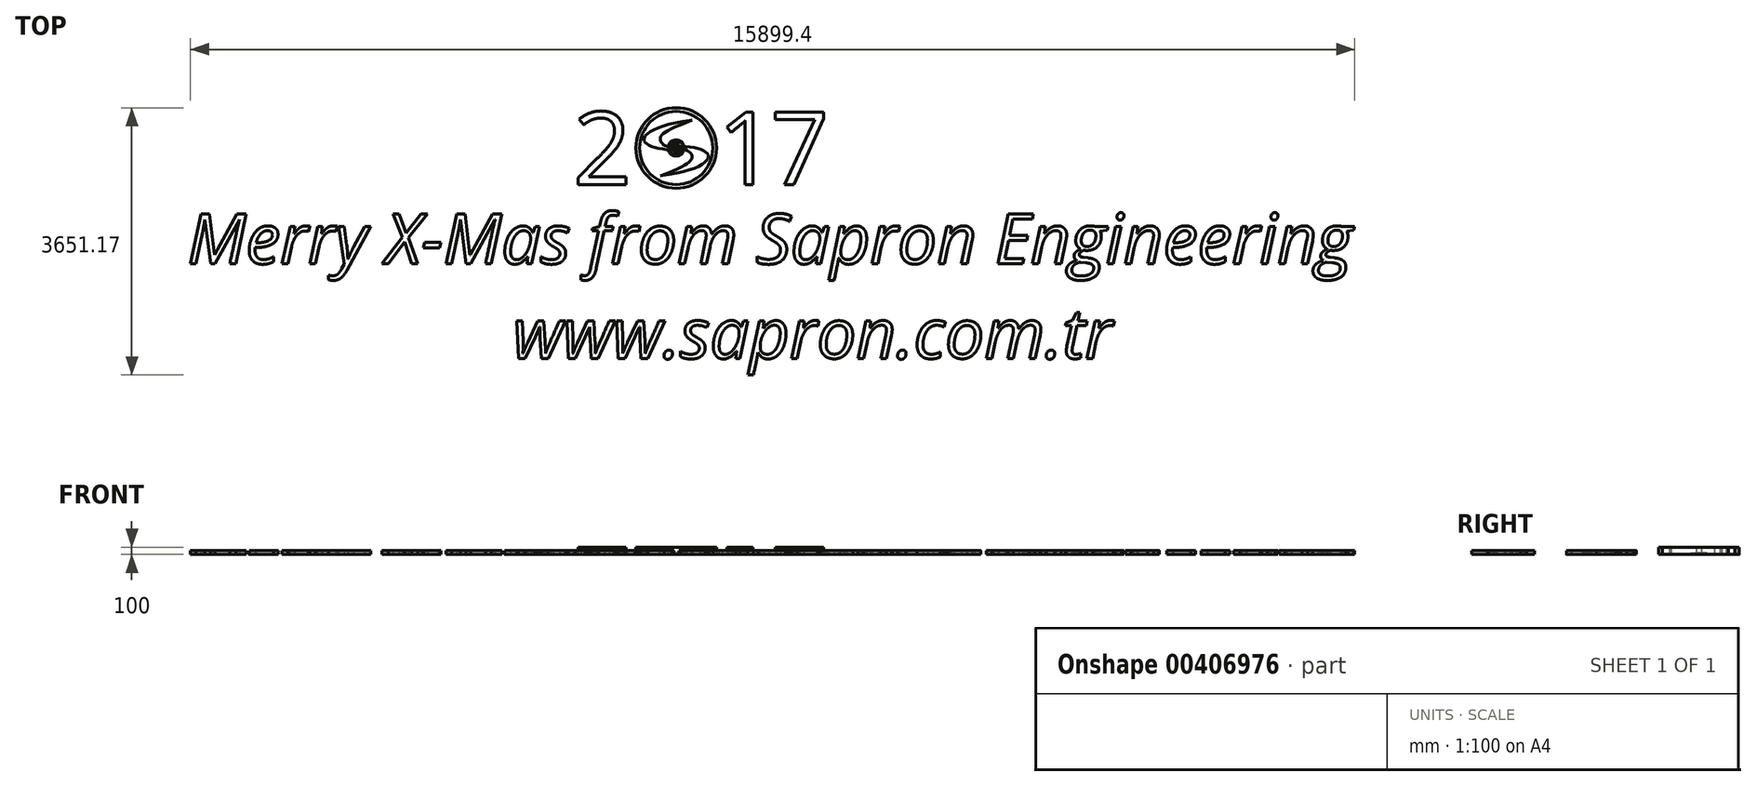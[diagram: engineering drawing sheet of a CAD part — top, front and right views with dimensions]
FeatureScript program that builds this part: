
annotation { "Feature Type Name" : "Feature", "Feature Type Description" : "" }
export const myFeature = defineFeature(function(context is Context, id is Id, definition is map)
    precondition{}
    {
        {
            var Q0;
            Q0=qCreatedBy(makeId("Top.planeOp"),FACE);
            var sketch = newSketch(context, id + "F0", { "sketchPlane" : qUnion([Q0])});
            skCircle(sketch, "E0", {"center": v(0, 0) * mm, "radius": 550 * mm});
            skCircle(sketch, "E1", {"center": v(0, 0) * mm, "radius": 500 * mm});
            skSolve(sketch);
        }
        {
            var Q0;
            Q0=qCreatedBy(makeId("Top.planeOp"),FACE);
            var sketch = newSketch(context, id + "F1", { "sketchPlane" : qUnion([Q0])});
            skText(sketch, "E2", { "text": "2", "fontName": "OpenSans-Regular.ttf"});
            skPoint(sketch, "E3", {"position": v(-1000, 0) * mm});
            const initialGuessF1  = {"E2": [-1.40484, -0.5, 1, 0, 1]};
            skSetInitialGuess(sketch, initialGuessF1);
            skSolve(sketch);
        }
        {
            var Q0;
            Q0=qCreatedBy(makeId("Top.planeOp"),FACE);
            var sketch = newSketch(context, id + "F2", { "sketchPlane" : qUnion([Q0])});
            skText(sketch, "E4", { "text": "1", "fontName": "OpenSans-Regular.ttf"});
            skPoint(sketch, "E5", {"position": v(850, 0) * mm});
            const initialGuessF2  = {"E4": [0.56257, -0.5, 1, 0, 1]};
            skSetInitialGuess(sketch, initialGuessF2);
            skSolve(sketch);
        }
        {
            var Q0;
            Q0=qCreatedBy(makeId("Top.planeOp"),FACE);
            var sketch = newSketch(context, id + "F3", { "sketchPlane" : qUnion([Q0])});
            skText(sketch, "E6", { "text": "7", "fontName": "OpenSans-Regular.ttf"});
            skPoint(sketch, "E7", {"position": v(1644.23, 0) * mm});
            skPoint(sketch, "E8", {"position": v(547.2, 0) * mm});
            skPoint(sketch, "E9", {"position": v(-547.73, 0) * mm});
            const initialGuessF3  = {"E6": [1.28743, -0.5, 1, 0, 1]};
            skSetInitialGuess(sketch, initialGuessF3);
            skSolve(sketch);
        }
        {
            var Q0;
            Q0=makeQuery(id+"F0.imprint","IMPRINT",FACE,{"disambiguationData":[TD([[makeQuery(id+"F0.imprint","IMPRINT",EDGE,{"derivedFrom":sQuery(id+"F0.wireOp",EDGE,"E0")}),1.0]])]});
            var Q1;
            Q1=makeQuery(id+"F1.imprint","IMPRINT",FACE,{"disambiguationData":[TD([[makeQuery(id+"F1.imprint","IMPRINT",EDGE,{"derivedFrom":sQuery(id+"F1.wireOp",EDGE,"E2.sketch_text.stroke-0")}),-1.0]])]});
            var Q2;
            Q2=makeQuery(id+"F2.imprint","IMPRINT",FACE,{"disambiguationData":[TD([[makeQuery(id+"F2.imprint","IMPRINT",EDGE,{"derivedFrom":sQuery(id+"F2.wireOp",EDGE,"E4.sketch_text.stroke-0")}),-1.0]])]});
            var Q3;
            Q3=makeQuery(id+"F3.imprint","IMPRINT",FACE,{"disambiguationData":[TD([[makeQuery(id+"F3.imprint","IMPRINT",EDGE,{"derivedFrom":sQuery(id+"F3.wireOp",EDGE,"E6.sketch_text.stroke-0")}),-1.0]])]});
            extrude(context, id + "F4", {"entities" : qUnion([Q0, Q1, Q2, Q3]), "depth" : 100 * mm});
        }
        {
            var Q0;
            Q0=qCreatedBy(makeId("Top.planeOp"),FACE);
            var sketch = newSketch(context, id + "F5", { "sketchPlane" : qUnion([Q0])});
            skPoint(sketch, "E10", {"position": v(235.96, 379.51) * mm});
            skPoint(sketch, "E11", {"position": v(-412.73, 89.64) * mm});
            skPoint(sketch, "E12", {"position": v(110.77, -36.28) * mm});
            skFitSpline(sketch, "E13", {"points": [v(235.96, 379.51) * mm, v(-412.73, 89.64) * mm, v(110.77, -36.28) * mm], "startDerivative": vector(-2842.12, -332.1) * mm, "endDerivative": vector(1785.84, -40.7) * mm});
            skPoint(sketch, "E14", {"position": v(-195.48, 106.23) * mm});
            skFitSpline(sketch, "E15", {"points": [v(235.96, 379.51) * mm, v(-195.48, 106.23) * mm, v(110.77, -36.28) * mm], "startDerivative": vector(-2236.59, -817.49) * mm, "endDerivative": vector(1737.9, -347.34) * mm});
            skSolve(sketch);
        }
        {
            var Q0;
            Q0=makeQuery(id+"F5.imprint","IMPRINT",FACE,{"disambiguationData":[TD([[makeQuery(id+"F5.imprint","IMPRINT",EDGE,{"derivedFrom":sQuery(id+"F5.wireOp",EDGE,"E13")}),1.0]])]});
            extrude(context, id + "F6", {"entities" : qUnion([Q0]), "depth" : 100 * mm});
        }
        {
            var Q0;
            Q0=qCreatedBy(makeId("Right.planeOp"),FACE);
            var sketch = newSketch(context, id + "F7", { "sketchPlane" : qUnion([Q0])});
            skLineSegment(sketch, "E16", {"start": v(0, 0) * mm, "end": v(0, -184.27) * mm});
            skSolve(sketch);
        }
        {
            var Q0;
            Q0=makeQuery(id+"F6.opExtrude","SWEPT_BODY",BODY,{"disambiguationData":[OSD([sQuery(id+"F5.wireOp",EDGE,"E13"),sQuery(id+"F5.wireOp",EDGE,"E15")])]});
            var Q1;
            Q1=sQuery(id+"F7.wireOp",EDGE,"E16");
            transform(context, id + "F8", {"entities" : qUnion([Q0]), "transformType" : TransformType.ROTATION, "transformAxis" : qUnion([Q1]), "angle" : 180 * degree, "makeCopy" : true});
        }
        {
            var Q0;
            Q0=makeQuery(id+"F6.opExtrude","SWEPT_BODY",BODY,{"disambiguationData":[OSD([sQuery(id+"F5.wireOp",EDGE,"E13"),sQuery(id+"F5.wireOp",EDGE,"E15")])]});
            transform(context, id + "F9", {"entities" : qUnion([Q0]), "transformType" : TransformType.TRANSLATION_3D, "dx" : -20 * mm, "dy" : 0 * mm, "dz" : 0 * mm, "makeCopy" : false});
        }
        {
            var Q0;
            Q0=makeQuery(id+"F8.opPattern","COPY",BODY,{"derivedFrom":makeQuery(id+"F6.opExtrude","SWEPT_BODY",BODY,{"disambiguationData":[OSD([sQuery(id+"F5.wireOp",EDGE,"E13"),sQuery(id+"F5.wireOp",EDGE,"E15")])]}),"instanceName":"1"});
            transform(context, id + "F10", {"entities" : qUnion([Q0]), "transformType" : TransformType.TRANSLATION_3D, "dx" : 20 * mm, "dy" : 0 * mm, "dz" : 0 * mm, "makeCopy" : false});
        }
        {
            var Q0;
            Q0=qCreatedBy(makeId("Top.planeOp"),FACE);
            var sketch = newSketch(context, id + "F11", { "sketchPlane" : qUnion([Q0])});
            skText(sketch, "E17", { "text": "Merry X-Mas from Sapron Engineering\n                  www.sapron.com.tr", "fontName": "OpenSans-Italic.ttf"});
            const initialGuessF11  = {"E17": [-6.67241, -1.58074, 1, 0, 0.68406]};
            skSetInitialGuess(sketch, initialGuessF11);
            skSolve(sketch);
        }
        {
            var Q0;
            Q0 = qSketchRegion(id + "F11", true);
            extrude(context, id + "F12", {"entities" : qUnion([Q0]), "depth" : 50 * mm});
        }
        {
            var Q0;
            Q0=makeQuery(id+"F8.opPattern","COPY",BODY,{"derivedFrom":makeQuery(id+"F6.opExtrude","SWEPT_BODY",BODY,{"disambiguationData":[OSD([sQuery(id+"F5.wireOp",EDGE,"E13"),sQuery(id+"F5.wireOp",EDGE,"E15")])]}),"instanceName":"1"});
            var Q1;
            Q1=makeQuery(id+"F4.opExtrude","SWEPT_BODY",BODY,{"disambiguationData":[OSD([sQuery(id+"F0.wireOp",EDGE,"E0"),sQuery(id+"F0.wireOp",EDGE,"E1")])]});
            var Q2;
            Q2=makeQuery(id+"F6.opExtrude","SWEPT_BODY",BODY,{"disambiguationData":[OSD([sQuery(id+"F5.wireOp",EDGE,"E13"),sQuery(id+"F5.wireOp",EDGE,"E15")])]});
            var Q3;
            Q3=sQuery(id+"F7.wireOp",VERTEX,"E16.start");
            transform(context, id + "F13", {"entities" : qUnion([Q0, Q1, Q2]), "transformType" : TransformType.SCALE_UNIFORMLY, "scale" : 0.2, "scalePoint" : qUnion([Q3]), "makeCopy" : true});
        }
    });
